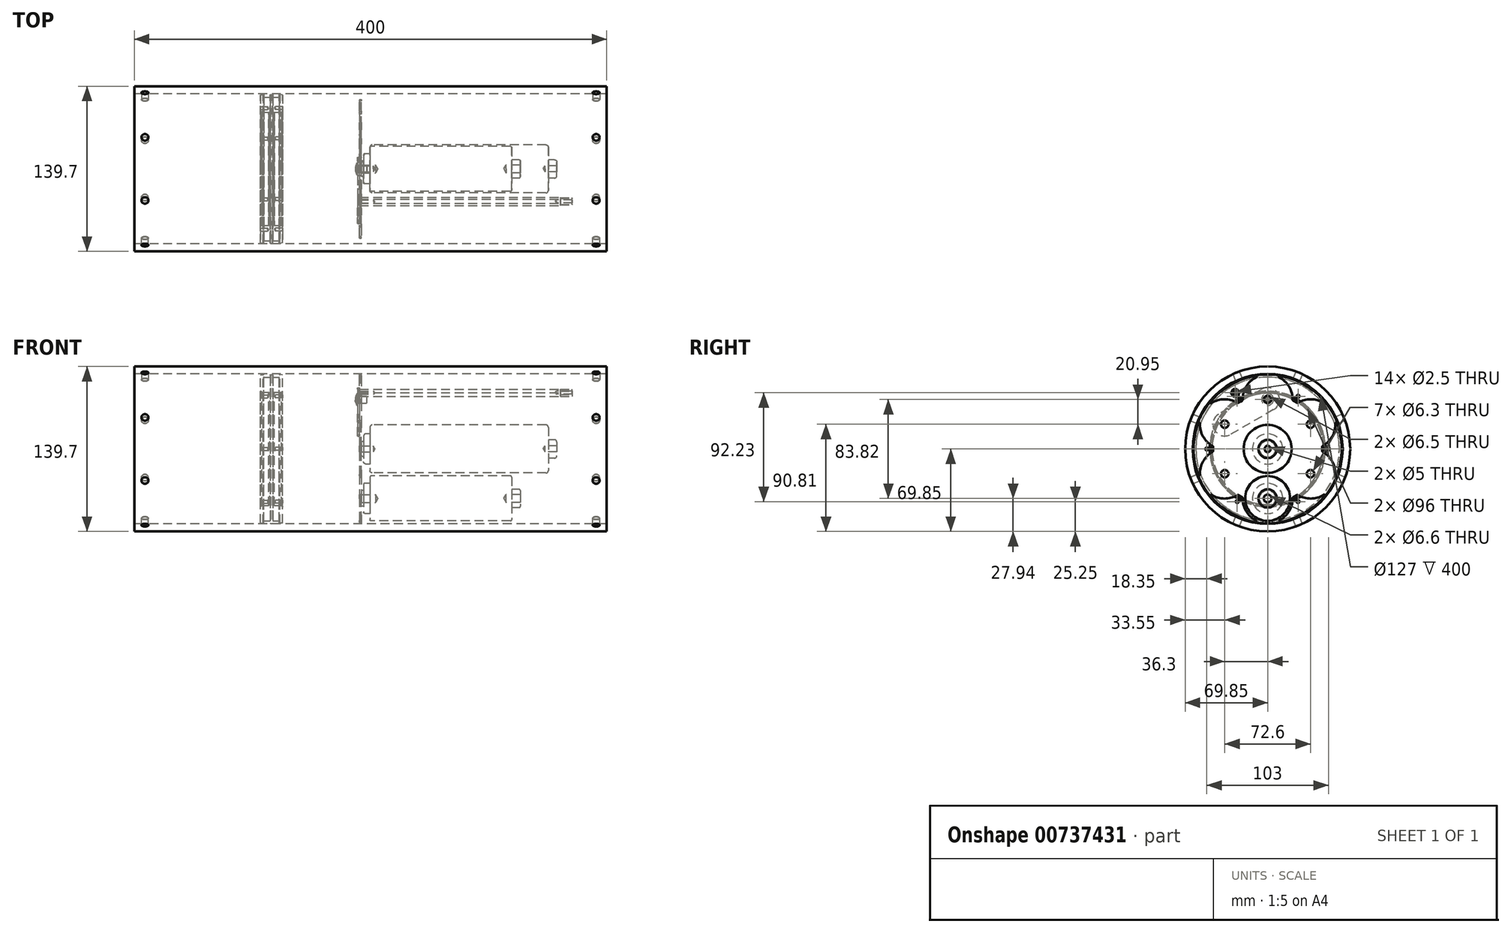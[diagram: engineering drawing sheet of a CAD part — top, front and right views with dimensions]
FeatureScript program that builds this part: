
annotation { "Feature Type Name" : "Feature", "Feature Type Description" : "" }
export const myFeature = defineFeature(function(context is Context, id is Id, definition is map)
    precondition{}
    {
        {
            var Q0;
            Q0=qCreatedBy(makeId("Front.planeOp"),FACE);
            var sketch = newSketch(context, id + "F0", { "sketchPlane" : qUnion([Q0])});
            skLineSegment(sketch, "E0", {"start": v(-82.75, 0) * mm, "end": v(82.75, 0) * mm});
            skLineSegment(sketch, "E1", {"start": v(-75.5, 20.32) * mm, "end": v(75.5, 20.32) * mm});
            skLineSegment(sketch, "E2", {"start": v(-82.75, 0) * mm, "end": v(-82.75, 6.75) * mm});
            skLineSegment(sketch, "E3", {"start": v(-82.75, 6.75) * mm, "end": v(-80.88, 6.75) * mm});
            skLineSegment(sketch, "E4", {"start": v(-80.88, 6.75) * mm, "end": v(-80.88, 12.8) * mm});
            skLineSegment(sketch, "E5", {"start": v(-80.88, 12.8) * mm, "end": v(-75.5, 12.8) * mm});
            skLineSegment(sketch, "E6", {"start": v(-75.5, 12.8) * mm, "end": v(-75.5, 20.32) * mm});
            skLineSegment(sketch, "E7", {"start": v(82.75, 0) * mm, "end": v(82.75, 7.75) * mm});
            skLineSegment(sketch, "E8", {"start": v(82.75, 7.75) * mm, "end": v(75.5, 7.75) * mm});
            skLineSegment(sketch, "E9", {"start": v(75.5, 7.75) * mm, "end": v(75.5, 20.32) * mm});
            skSolve(sketch);
        }
        {
            var Q0;
            Q0=makeQuery(id+"F0.imprint","IMPRINT",FACE,{"disambiguationData":[TD([[makeQuery(id+"F0.imprint","IMPRINT",EDGE,{"derivedFrom":sQuery(id+"F0.wireOp",EDGE,"E0")}),1.0]])]});
            var Q1;
            Q1=sQuery(id+"F0.wireOp",EDGE,"E0");
            revolve(context, id + "F1", {"entities" : qUnion([Q0]), "axis" : qUnion([Q1]), "revolveType" : RevolveType.FULL});
        }
        {
            var Q0;
            Q0=makeQuery(id+"F1.opRevolve","SWEPT_FACE",FACE,{"disambiguationData":[OSD([sQuery(id+"F0.wireOp",EDGE,"E1")])]});
            var Q1;
            Q1=makeQuery(id+"F1.opRevolve","SWEPT_EDGE",EDGE,{"disambiguationData":[OSD([sQuery(id+"F0.wireOp",EDGE,"E7"),sQuery(id+"F0.wireOp",EDGE,"E8")])]});
            var Q2;
            Q2=makeQuery(id+"F1.opRevolve","SWEPT_EDGE",EDGE,{"disambiguationData":[OSD([sQuery(id+"F0.wireOp",EDGE,"E4"),sQuery(id+"F0.wireOp",EDGE,"E5")])]});
            var Q3;
            Q3=makeQuery(id+"F1.opRevolve","SWEPT_EDGE",EDGE,{"disambiguationData":[OSD([sQuery(id+"F0.wireOp",EDGE,"E2"),sQuery(id+"F0.wireOp",EDGE,"E3")])]});
            fillet(context, id + "F2", {"entities" : qUnion([Q0, Q1, Q2, Q3]), "radius" : 2 * mm, "tangentPropagation" : true, "allowEdgeOverflow" : false});
        }
        {
            var Q0;
            Q0=makeQuery(id+"F1.opRevolve","SWEPT_FACE",FACE,{"disambiguationData":[OSD([sQuery(id+"F0.wireOp",EDGE,"E2")])]});
            var sketch = newSketch(context, id + "F3", { "sketchPlane" : qUnion([Q0])});
            skPoint(sketch, "E10", {"position": v(0, 0) * mm});
            skSolve(sketch);
        }
        {
            var Q0;
            Q0=makeQuery(id+"F1.opRevolve","SWEPT_FACE",FACE,{"disambiguationData":[OSD([sQuery(id+"F0.wireOp",EDGE,"E7")])]});
            var sketch = newSketch(context, id + "F4", { "sketchPlane" : qUnion([Q0])});
            skPoint(sketch, "E11", {"position": v(0, 0) * mm});
            skSolve(sketch);
        }
        {
            var Q0;
            Q0=sQuery(id+"F4.wireOp",VERTEX,"E11");
            var Q1;
            Q1=sQuery(id+"F3.wireOp",VERTEX,"E10");
            var Q2;
            Q2=makeQuery(id+"F1.opRevolve","SWEPT_BODY",BODY,{"disambiguationData":[OSD([sQuery(id+"F0.wireOp",EDGE,"E0"),sQuery(id+"F0.wireOp",EDGE,"E1"),sQuery(id+"F0.wireOp",EDGE,"E2"),sQuery(id+"F0.wireOp",EDGE,"E3"),sQuery(id+"F0.wireOp",EDGE,"E4"),sQuery(id+"F0.wireOp",EDGE,"E5"),sQuery(id+"F0.wireOp",EDGE,"E6"),sQuery(id+"F0.wireOp",EDGE,"E7"),sQuery(id+"F0.wireOp",EDGE,"E8"),sQuery(id+"F0.wireOp",EDGE,"E9")])]});
            hole(context, id + "F5", {"style" : HoleStyle.SIMPLE, "endStyle" : HoleEndStyle.BLIND, "standardTappedOrClearance" : lookupTablePath({ "standard" : "ISO", "engagement" : "75%", "pitch" : "1 mm", "size" : "M6", "type" : "Tapped" }), "standardBlindInLast" : lookupTablePath({ "standard" : "ISO", "engagement" : "75%", "pitch" : "1 mm", "size" : "M6", "type" : "Tapped" }), "holeDiameter" : 5 * mm, "holeDepth" : 10 * mm, "locations" : qUnion([Q0, Q1]), "scope" : qUnion([Q2]), "majorDiameter" : 6 * mm});
        }
        {
            var Q0;
            Q0=makeQuery(id+"F1.opRevolve","SWEPT_FACE",FACE,{"disambiguationData":[OSD([sQuery(id+"F0.wireOp",EDGE,"E2")])]});
            var sketch = newSketch(context, id + "F6", { "sketchPlane" : qUnion([Q0])});
            skCircle(sketch, "E12", {"center": v(0, 0) * mm, "radius": 63.5 * mm, "construction": true});
            skCircle(sketch, "E13.0", {"center": v(0, 0) * mm, "radius": 20.32 * mm, "construction": true});
            skLineSegment(sketch, "E14", {"start": v(0, 20.32) * mm, "end": v(0, 63.5) * mm, "construction": true});
            skCircle(sketch, "E15", {"center": v(0, 41.91) * mm, "radius": 20.32 * mm, "construction": true});
            skCircle(sketch, "E16", {"center": v(0, 41.91) * mm, "radius": 3.15 * mm});
            skCircle(sketch, "E17", {"center": v(0, 0) * mm, "radius": 3.15 * mm});
            skCircle(sketch, "E18", {"center": v(0, 0) * mm, "radius": 63 * mm});
            skCircle(sketch, "E19.1.0", {"center": v(-36.3, 20.96) * mm, "radius": 3.15 * mm});
            skCircle(sketch, "E19.2.0", {"center": v(-36.3, -20.96) * mm, "radius": 3.15 * mm});
            skCircle(sketch, "E19.3.0", {"center": v(0, -41.91) * mm, "radius": 3.15 * mm});
            skCircle(sketch, "E19.4.0", {"center": v(36.3, -20.96) * mm, "radius": 3.15 * mm});
            skCircle(sketch, "E19.5.0", {"center": v(36.3, 20.96) * mm, "radius": 3.15 * mm});
            skCircle(sketch, "E20", {"center": v(36.3, 20.96) * mm, "radius": 20.32 * mm, "construction": true});
            skCircle(sketch, "E21", {"center": v(0, 41.91) * mm, "radius": 10 * mm, "construction": true});
            skCircle(sketch, "E22", {"center": v(36.3, 20.96) * mm, "radius": 10 * mm, "construction": true});
            skLineSegment(sketch, "E23", {"start": v(-5, 33.25) * mm, "end": v(31.3, 12.3) * mm, "construction": true});
            skLineSegment(sketch, "E24", {"start": v(5, 50.57) * mm, "end": v(41.3, 29.62) * mm, "construction": true});
            skArc(sketch, "E25", {"start": v(0, 63) * mm, "mid": v(15.13, 56.6) * mm, "end": v(21.08, 41.29) * mm});
            skLineSegment(sketch, "E26", {"start": v(23.15, 40.1) * mm, "end": v(35.3, 61.15) * mm, "construction": true});
            skArc(sketch, "E27.MirrorCS", {"start": v(54.56, 31.5) * mm, "mid": v(41.45, 41.4) * mm, "end": v(25.22, 38.9) * mm});
            skLineSegment(sketch, "E28", {"start": v(21.08, 41.29) * mm, "end": v(25.22, 38.9) * mm});
            skLineSegment(sketch, "E29", {"start": v(9.66, 62.25) * mm, "end": v(9.43, 60.77) * mm});
            skCircle(sketch, "E30", {"center": v(0, -41.91) * mm, "radius": 19 * mm, "construction": true});
            skCircle(sketch, "E31", {"center": v(-36.3, -20.96) * mm, "radius": 19 * mm, "construction": true});
            skSolve(sketch);
        }
        {
            var Q0;
            Q0=qSketchRegion(id+"F6",true);
            extrude(context, id + "F7", {"entities" : qUnion([Q0]), "depth" : 1.6 * mm});
        }
        {
            var Q0;
            Q0=makeQuery(id+"F7.opExtrude","CAP_FACE",FACE,{"disambiguationData":[OSD([sQuery(id+"F6.wireOp",EDGE,"E16"),sQuery(id+"F6.wireOp",EDGE,"E17"),sQuery(id+"F6.wireOp",EDGE,"E18"),sQuery(id+"F6.wireOp",EDGE,"E19.1.0"),sQuery(id+"F6.wireOp",EDGE,"E19.2.0"),sQuery(id+"F6.wireOp",EDGE,"E19.3.0"),sQuery(id+"F6.wireOp",EDGE,"E19.4.0"),sQuery(id+"F6.wireOp",EDGE,"E19.5.0")])],"isStart":false});
            var sketch = newSketch(context, id + "F8", { "sketchPlane" : qUnion([Q0])});
            skArc(sketch, "E32.0", {"start": v(9.94, 60.51) * mm, "mid": v(18.13, 52.69) * mm, "end": v(21.09, 41.75) * mm});
            skArc(sketch, "E32.1", {"start": v(47.44, 38.86) * mm, "mid": v(36.57, 42.04) * mm, "end": v(25.62, 39.14) * mm});
            skArc(sketch, "E32.2", {"start": v(49.08, 39.5) * mm, "mid": v(31.5, 54.56) * mm, "end": v(9.66, 62.25) * mm});
            skLineSegment(sketch, "E32.3", {"start": v(9.66, 62.25) * mm, "end": v(9.52, 61.34) * mm});
            skLineSegment(sketch, "E32.4", {"start": v(21.49, 41.05) * mm, "end": v(24.81, 39.14) * mm});
            skLineSegment(sketch, "E32.5", {"start": v(23.15, 40.1) * mm, "end": v(35.3, 61.15) * mm, "construction": true});
            skLineSegment(sketch, "E33.MirrorCS", {"start": v(49.08, 39.5) * mm, "end": v(48.36, 38.92) * mm});
            skPoint(sketch, "E34.orphan", {"position": v(54.56, 31.5) * mm});
            skPoint(sketch, "E35.orphan", {"position": v(0, 63) * mm});
            skPoint(sketch, "E36.visualSharp", {"position": v(21.08, 41.29) * mm});
            skArc(sketch, "E36.filletArc", {"start": v(21.09, 41.75) * mm, "mid": v(21.2, 41.35) * mm, "end": v(21.49, 41.05) * mm});
            skPoint(sketch, "E37.visualSharp", {"position": v(25.22, 38.9) * mm});
            skArc(sketch, "E37.filletArc", {"start": v(24.81, 39.14) * mm, "mid": v(25.21, 39.03) * mm, "end": v(25.62, 39.14) * mm});
            skPoint(sketch, "E38.visualSharp", {"position": v(47.91, 38.56) * mm});
            skArc(sketch, "E38.filletArc", {"start": v(47.44, 38.86) * mm, "mid": v(47.9, 38.74) * mm, "end": v(48.36, 38.92) * mm});
            skPoint(sketch, "E39.visualSharp", {"position": v(9.43, 60.77) * mm});
            skArc(sketch, "E39.filletArc", {"start": v(9.52, 61.34) * mm, "mid": v(9.6, 60.86) * mm, "end": v(9.94, 60.51) * mm});
            skPoint(sketch, "E40.1.1", {"position": v(-54.56, 31.5) * mm});
            skArc(sketch, "E40.1.2", {"start": v(-47.44, 38.86) * mm, "mid": v(-36.57, 42.04) * mm, "end": v(-25.62, 39.14) * mm});
            skArc(sketch, "E40.1.3", {"start": v(-9.94, 60.51) * mm, "mid": v(-18.13, 52.69) * mm, "end": v(-21.09, 41.75) * mm});
            skArc(sketch, "E40.1.4", {"start": v(-9.66, 62.25) * mm, "mid": v(-31.5, 54.56) * mm, "end": v(-49.08, 39.5) * mm});
            skLineSegment(sketch, "E40.1.5", {"start": v(-23.15, 40.1) * mm, "end": v(-35.3, 61.15) * mm, "construction": true});
            skPoint(sketch, "E40.1.6", {"position": v(-25.22, 38.9) * mm});
            skPoint(sketch, "E40.1.7", {"position": v(-21.08, 41.29) * mm});
            skPoint(sketch, "E40.1.8", {"position": v(-9.43, 60.77) * mm});
            skPoint(sketch, "E40.1.9", {"position": v(-47.91, 38.56) * mm});
            skLineSegment(sketch, "E40.1.10", {"start": v(-24.81, 39.14) * mm, "end": v(-21.49, 41.05) * mm});
            skArc(sketch, "E40.1.11", {"start": v(-48.36, 38.92) * mm, "mid": v(-47.9, 38.74) * mm, "end": v(-47.44, 38.86) * mm});
            skLineSegment(sketch, "E40.1.12", {"start": v(-49.08, 39.5) * mm, "end": v(-48.36, 38.92) * mm});
            skArc(sketch, "E40.1.13", {"start": v(-25.62, 39.14) * mm, "mid": v(-25.21, 39.03) * mm, "end": v(-24.81, 39.14) * mm});
            skArc(sketch, "E40.1.14", {"start": v(-21.49, 41.05) * mm, "mid": v(-21.2, 41.35) * mm, "end": v(-21.09, 41.75) * mm});
            skLineSegment(sketch, "E40.1.15", {"start": v(-9.66, 62.25) * mm, "end": v(-9.52, 61.34) * mm});
            skArc(sketch, "E40.1.16", {"start": v(-9.94, 60.51) * mm, "mid": v(-9.6, 60.86) * mm, "end": v(-9.52, 61.34) * mm});
            skPoint(sketch, "E40.2.0", {"position": v(-54.56, 31.5) * mm});
            skPoint(sketch, "E40.2.1", {"position": v(-54.56, -31.5) * mm});
            skArc(sketch, "E40.2.2", {"start": v(-57.37, -21.65) * mm, "mid": v(-54.7, -10.65) * mm, "end": v(-46.7, -2.61) * mm});
            skArc(sketch, "E40.2.3", {"start": v(-57.37, 21.65) * mm, "mid": v(-54.7, 10.65) * mm, "end": v(-46.7, 2.61) * mm});
            skArc(sketch, "E40.2.4", {"start": v(-58.75, 22.76) * mm, "mid": v(-63, 0) * mm, "end": v(-58.75, -22.76) * mm});
            skLineSegment(sketch, "E40.2.5", {"start": v(-46.3, 0) * mm, "end": v(-70.6, 0) * mm, "construction": true});
            skPoint(sketch, "E40.2.6", {"position": v(-46.3, -2.4) * mm});
            skPoint(sketch, "E40.2.7", {"position": v(-46.3, 2.4) * mm});
            skPoint(sketch, "E40.2.8", {"position": v(-57.35, 22.22) * mm});
            skPoint(sketch, "E40.2.9", {"position": v(-57.35, -22.22) * mm});
            skLineSegment(sketch, "E40.2.10", {"start": v(-46.3, -1.92) * mm, "end": v(-46.3, 1.92) * mm});
            skArc(sketch, "E40.2.11", {"start": v(-57.88, -22.42) * mm, "mid": v(-57.5, -22.12) * mm, "end": v(-57.37, -21.65) * mm});
            skLineSegment(sketch, "E40.2.12", {"start": v(-58.75, -22.76) * mm, "end": v(-57.88, -22.42) * mm});
            skArc(sketch, "E40.2.13", {"start": v(-46.7, -2.61) * mm, "mid": v(-46.4, -2.32) * mm, "end": v(-46.3, -1.92) * mm});
            skArc(sketch, "E40.2.14", {"start": v(-46.3, 1.92) * mm, "mid": v(-46.4, 2.32) * mm, "end": v(-46.7, 2.61) * mm});
            skLineSegment(sketch, "E40.2.15", {"start": v(-58.75, 22.76) * mm, "end": v(-57.88, 22.42) * mm});
            skArc(sketch, "E40.2.16", {"start": v(-57.37, 21.65) * mm, "mid": v(-57.5, 22.12) * mm, "end": v(-57.88, 22.42) * mm});
            skPoint(sketch, "E40.3.0", {"position": v(-54.56, -31.5) * mm});
            skPoint(sketch, "E40.3.1", {"position": v(0, -63) * mm});
            skArc(sketch, "E40.3.2", {"start": v(-9.94, -60.51) * mm, "mid": v(-18.13, -52.69) * mm, "end": v(-21.09, -41.75) * mm});
            skArc(sketch, "E40.3.3", {"start": v(-47.44, -38.86) * mm, "mid": v(-36.57, -42.04) * mm, "end": v(-25.62, -39.14) * mm});
            skArc(sketch, "E40.3.4", {"start": v(-49.08, -39.5) * mm, "mid": v(-31.5, -54.56) * mm, "end": v(-9.66, -62.25) * mm});
            skLineSegment(sketch, "E40.3.5", {"start": v(-23.15, -40.1) * mm, "end": v(-35.3, -61.15) * mm, "construction": true});
            skPoint(sketch, "E40.3.6", {"position": v(-21.08, -41.29) * mm});
            skPoint(sketch, "E40.3.7", {"position": v(-25.22, -38.9) * mm});
            skPoint(sketch, "E40.3.8", {"position": v(-47.91, -38.56) * mm});
            skPoint(sketch, "E40.3.9", {"position": v(-9.43, -60.77) * mm});
            skLineSegment(sketch, "E40.3.10", {"start": v(-21.49, -41.05) * mm, "end": v(-24.81, -39.14) * mm});
            skArc(sketch, "E40.3.11", {"start": v(-9.52, -61.34) * mm, "mid": v(-9.6, -60.86) * mm, "end": v(-9.94, -60.51) * mm});
            skLineSegment(sketch, "E40.3.12", {"start": v(-9.66, -62.25) * mm, "end": v(-9.52, -61.34) * mm});
            skArc(sketch, "E40.3.13", {"start": v(-21.09, -41.75) * mm, "mid": v(-21.2, -41.35) * mm, "end": v(-21.49, -41.05) * mm});
            skArc(sketch, "E40.3.14", {"start": v(-24.81, -39.14) * mm, "mid": v(-25.21, -39.03) * mm, "end": v(-25.62, -39.14) * mm});
            skLineSegment(sketch, "E40.3.15", {"start": v(-49.08, -39.5) * mm, "end": v(-48.36, -38.92) * mm});
            skArc(sketch, "E40.3.16", {"start": v(-47.44, -38.86) * mm, "mid": v(-47.9, -38.74) * mm, "end": v(-48.36, -38.92) * mm});
            skPoint(sketch, "E40.4.0", {"position": v(0, -63) * mm});
            skPoint(sketch, "E40.4.1", {"position": v(54.56, -31.5) * mm});
            skArc(sketch, "E40.4.2", {"start": v(47.44, -38.86) * mm, "mid": v(36.57, -42.04) * mm, "end": v(25.62, -39.14) * mm});
            skArc(sketch, "E40.4.3", {"start": v(9.94, -60.51) * mm, "mid": v(18.13, -52.69) * mm, "end": v(21.09, -41.75) * mm});
            skArc(sketch, "E40.4.4", {"start": v(9.66, -62.25) * mm, "mid": v(31.5, -54.56) * mm, "end": v(49.08, -39.5) * mm});
            skLineSegment(sketch, "E40.4.5", {"start": v(23.15, -40.1) * mm, "end": v(35.3, -61.15) * mm, "construction": true});
            skPoint(sketch, "E40.4.6", {"position": v(25.22, -38.9) * mm});
            skPoint(sketch, "E40.4.7", {"position": v(21.08, -41.29) * mm});
            skPoint(sketch, "E40.4.8", {"position": v(9.43, -60.77) * mm});
            skPoint(sketch, "E40.4.9", {"position": v(47.91, -38.56) * mm});
            skLineSegment(sketch, "E40.4.10", {"start": v(24.81, -39.14) * mm, "end": v(21.49, -41.05) * mm});
            skArc(sketch, "E40.4.11", {"start": v(48.36, -38.92) * mm, "mid": v(47.9, -38.74) * mm, "end": v(47.44, -38.86) * mm});
            skLineSegment(sketch, "E40.4.12", {"start": v(49.08, -39.5) * mm, "end": v(48.36, -38.92) * mm});
            skArc(sketch, "E40.4.13", {"start": v(25.62, -39.14) * mm, "mid": v(25.21, -39.03) * mm, "end": v(24.81, -39.14) * mm});
            skArc(sketch, "E40.4.14", {"start": v(21.49, -41.05) * mm, "mid": v(21.2, -41.35) * mm, "end": v(21.09, -41.75) * mm});
            skLineSegment(sketch, "E40.4.15", {"start": v(9.66, -62.25) * mm, "end": v(9.52, -61.34) * mm});
            skArc(sketch, "E40.4.16", {"start": v(9.94, -60.51) * mm, "mid": v(9.6, -60.86) * mm, "end": v(9.52, -61.34) * mm});
            skPoint(sketch, "E40.5.0", {"position": v(54.56, -31.5) * mm});
            skArc(sketch, "E40.5.2", {"start": v(57.37, 21.65) * mm, "mid": v(54.7, 10.65) * mm, "end": v(46.7, 2.61) * mm});
            skArc(sketch, "E40.5.3", {"start": v(57.37, -21.65) * mm, "mid": v(54.7, -10.65) * mm, "end": v(46.7, -2.61) * mm});
            skArc(sketch, "E40.5.4", {"start": v(58.75, -22.76) * mm, "mid": v(63, 0) * mm, "end": v(58.75, 22.76) * mm});
            skLineSegment(sketch, "E40.5.5", {"start": v(46.3, 0) * mm, "end": v(70.6, 0) * mm, "construction": true});
            skPoint(sketch, "E40.5.6", {"position": v(46.3, 2.4) * mm});
            skPoint(sketch, "E40.5.7", {"position": v(46.3, -2.4) * mm});
            skPoint(sketch, "E40.5.8", {"position": v(57.35, -22.22) * mm});
            skPoint(sketch, "E40.5.9", {"position": v(57.35, 22.22) * mm});
            skLineSegment(sketch, "E40.5.10", {"start": v(46.3, 1.92) * mm, "end": v(46.3, -1.92) * mm});
            skArc(sketch, "E40.5.11", {"start": v(57.88, 22.42) * mm, "mid": v(57.5, 22.12) * mm, "end": v(57.37, 21.65) * mm});
            skLineSegment(sketch, "E40.5.12", {"start": v(58.75, 22.76) * mm, "end": v(57.88, 22.42) * mm});
            skArc(sketch, "E40.5.13", {"start": v(46.7, 2.61) * mm, "mid": v(46.4, 2.32) * mm, "end": v(46.3, 1.92) * mm});
            skArc(sketch, "E40.5.14", {"start": v(46.3, -1.92) * mm, "mid": v(46.4, -2.32) * mm, "end": v(46.7, -2.61) * mm});
            skLineSegment(sketch, "E40.5.15", {"start": v(58.75, -22.76) * mm, "end": v(57.88, -22.42) * mm});
            skArc(sketch, "E40.5.16", {"start": v(57.37, -21.65) * mm, "mid": v(57.5, -22.12) * mm, "end": v(57.88, -22.42) * mm});
            skSolve(sketch);
        }
        {
            var Q0;
            Q0=qSketchRegion(id+"F8",true);
            extrude(context, id + "F9", {"entities" : qUnion([Q0]), "operationType" : NewBodyOperationType.REMOVE, "oppositeDirection" : true, "depth" : 25 * mm});
        }
        {
            var Q0;
            Q0=makeQuery(id+"F9.boolean.opBoolean","COPY",EDGE,{"derivedFrom":makeQuery(id+"F9.opExtrude","SWEPT_EDGE",EDGE,{"disambiguationData":[OSD([sQuery(id+"F6.wireOp",EDGE,"E18"),sQuery(id+"F8.wireOp",EDGE,"E32.2"),sQuery(id+"F8.wireOp",EDGE,"E32.3")])]})});
            var Q1;
            Q1=makeQuery(id+"F9.boolean.opBoolean","COPY",EDGE,{"derivedFrom":makeQuery(id+"F9.opExtrude","SWEPT_EDGE",EDGE,{"disambiguationData":[OSD([sQuery(id+"F6.wireOp",EDGE,"E18"),sQuery(id+"F8.wireOp",EDGE,"E32.2"),sQuery(id+"F8.wireOp",EDGE,"E33.MirrorCS")])]})});
            var Q2;
            Q2=makeQuery(id+"FGbRxVnL68Y7Bjd_2.1.F9.boolean.opBoolean","COPY",EDGE,{"derivedFrom":makeQuery(id+"FGbRxVnL68Y7Bjd_2.1.F9.opExtrude","SWEPT_EDGE",EDGE,{"disambiguationData":[OSD([sQuery(id+"F6.wireOp",EDGE,"E18"),sQuery(id+"F8.wireOp",EDGE,"E32.2"),sQuery(id+"F8.wireOp",EDGE,"E32.3")])]})});
            var Q3;
            Q3=makeQuery(id+"FGbRxVnL68Y7Bjd_2.1.F9.boolean.opBoolean","COPY",EDGE,{"derivedFrom":makeQuery(id+"FGbRxVnL68Y7Bjd_2.1.F9.opExtrude","SWEPT_EDGE",EDGE,{"disambiguationData":[OSD([sQuery(id+"F6.wireOp",EDGE,"E18"),sQuery(id+"F8.wireOp",EDGE,"E32.2"),sQuery(id+"F8.wireOp",EDGE,"E33.MirrorCS")])]})});
            var Q4;
            Q4=makeQuery(id+"FGbRxVnL68Y7Bjd_2.2.F9.boolean.opBoolean","COPY",EDGE,{"derivedFrom":makeQuery(id+"FGbRxVnL68Y7Bjd_2.2.F9.opExtrude","SWEPT_EDGE",EDGE,{"disambiguationData":[OSD([sQuery(id+"F6.wireOp",EDGE,"E18"),sQuery(id+"F8.wireOp",EDGE,"E32.2"),sQuery(id+"F8.wireOp",EDGE,"E32.3")])]})});
            var Q5;
            Q5=makeQuery(id+"FGbRxVnL68Y7Bjd_2.2.F9.boolean.opBoolean","COPY",EDGE,{"derivedFrom":makeQuery(id+"FGbRxVnL68Y7Bjd_2.2.F9.opExtrude","SWEPT_EDGE",EDGE,{"disambiguationData":[OSD([sQuery(id+"F6.wireOp",EDGE,"E18"),sQuery(id+"F8.wireOp",EDGE,"E32.2"),sQuery(id+"F8.wireOp",EDGE,"E33.MirrorCS")])]})});
            var Q6;
            Q6=makeQuery(id+"FGbRxVnL68Y7Bjd_2.3.F9.boolean.opBoolean","COPY",EDGE,{"derivedFrom":makeQuery(id+"FGbRxVnL68Y7Bjd_2.3.F9.opExtrude","SWEPT_EDGE",EDGE,{"disambiguationData":[OSD([sQuery(id+"F6.wireOp",EDGE,"E18"),sQuery(id+"F8.wireOp",EDGE,"E32.2"),sQuery(id+"F8.wireOp",EDGE,"E32.3")])]})});
            var Q7;
            Q7=makeQuery(id+"FGbRxVnL68Y7Bjd_2.4.F9.boolean.opBoolean","COPY",EDGE,{"derivedFrom":makeQuery(id+"FGbRxVnL68Y7Bjd_2.4.F9.opExtrude","SWEPT_EDGE",EDGE,{"disambiguationData":[OSD([sQuery(id+"F6.wireOp",EDGE,"E18"),sQuery(id+"F8.wireOp",EDGE,"E32.2"),sQuery(id+"F8.wireOp",EDGE,"E32.3")])]})});
            var Q8;
            Q8=makeQuery(id+"FGbRxVnL68Y7Bjd_2.3.F9.boolean.opBoolean","COPY",EDGE,{"derivedFrom":makeQuery(id+"FGbRxVnL68Y7Bjd_2.3.F9.opExtrude","SWEPT_EDGE",EDGE,{"disambiguationData":[OSD([sQuery(id+"F6.wireOp",EDGE,"E18"),sQuery(id+"F8.wireOp",EDGE,"E32.2"),sQuery(id+"F8.wireOp",EDGE,"E33.MirrorCS")])]})});
            var Q9;
            Q9=makeQuery(id+"FGbRxVnL68Y7Bjd_2.4.F9.boolean.opBoolean","COPY",EDGE,{"derivedFrom":makeQuery(id+"FGbRxVnL68Y7Bjd_2.4.F9.opExtrude","SWEPT_EDGE",EDGE,{"disambiguationData":[OSD([sQuery(id+"F6.wireOp",EDGE,"E18"),sQuery(id+"F8.wireOp",EDGE,"E32.2"),sQuery(id+"F8.wireOp",EDGE,"E33.MirrorCS")])]})});
            var Q10;
            Q10=makeQuery(id+"FGbRxVnL68Y7Bjd_2.5.F9.boolean.opBoolean","COPY",EDGE,{"derivedFrom":makeQuery(id+"FGbRxVnL68Y7Bjd_2.5.F9.opExtrude","SWEPT_EDGE",EDGE,{"disambiguationData":[OSD([sQuery(id+"F6.wireOp",EDGE,"E18"),sQuery(id+"F8.wireOp",EDGE,"E32.2"),sQuery(id+"F8.wireOp",EDGE,"E32.3")])]})});
            var Q11;
            Q11=makeQuery(id+"FGbRxVnL68Y7Bjd_2.5.F9.boolean.opBoolean","COPY",EDGE,{"derivedFrom":makeQuery(id+"FGbRxVnL68Y7Bjd_2.5.F9.opExtrude","SWEPT_EDGE",EDGE,{"disambiguationData":[OSD([sQuery(id+"F6.wireOp",EDGE,"E18"),sQuery(id+"F8.wireOp",EDGE,"E32.2"),sQuery(id+"F8.wireOp",EDGE,"E33.MirrorCS")])]})});
            fillet(context, id + "F10", {"entities" : qUnion([Q0, Q1, Q2, Q3, Q4, Q5, Q6, Q7, Q8, Q9, Q10, Q11]), "radius" : .8 * mm, "tangentPropagation" : true, "allowEdgeOverflow" : false});
        }
        {
            var Q0;
            Q0=makeQuery(id+"F7.opExtrude","CAP_FACE",FACE,{"disambiguationData":[OSD([sQuery(id+"F6.wireOp",EDGE,"E16"),sQuery(id+"F6.wireOp",EDGE,"E17"),sQuery(id+"F6.wireOp",EDGE,"E18"),sQuery(id+"F6.wireOp",EDGE,"E19.1.0"),sQuery(id+"F6.wireOp",EDGE,"E19.2.0"),sQuery(id+"F6.wireOp",EDGE,"E19.3.0"),sQuery(id+"F6.wireOp",EDGE,"E19.4.0"),sQuery(id+"F6.wireOp",EDGE,"E19.5.0")])],"isStart":false});
            var sketch = newSketch(context, id + "F11", { "sketchPlane" : qUnion([Q0])});
            skLineSegment(sketch, "E41.0", {"start": v(-5, 33.25) * mm, "end": v(31.3, 12.3) * mm});
            skLineSegment(sketch, "E41.1", {"start": v(5, 50.57) * mm, "end": v(41.3, 29.62) * mm});
            skArc(sketch, "E41.2", {"start": v(5, 50.57) * mm, "mid": v(-8.66, 46.91) * mm, "end": v(-5, 33.25) * mm});
            skArc(sketch, "E41.3", {"start": v(31.3, 12.3) * mm, "mid": v(44.96, 15.96) * mm, "end": v(41.3, 29.62) * mm});
            skPoint(sketch, "E41.4", {"position": v(0, 41.91) * mm});
            skPoint(sketch, "E41.5", {"position": v(36.3, 20.96) * mm});
            skCircle(sketch, "E42", {"center": v(0, 41.91) * mm, "radius": 3.25 * mm});
            skCircle(sketch, "E43", {"center": v(36.3, 20.96) * mm, "radius": 3.25 * mm});
            skSolve(sketch);
        }
        {
            var Q0;
            Q0=makeQuery(id+"F11.imprint","IMPRINT",FACE,{"disambiguationData":[TD([[makeQuery(id+"F11.imprint","IMPRINT",EDGE,{"derivedFrom":sQuery(id+"F11.wireOp",EDGE,"E41.0")}),1.0]])]});
            extrude(context, id + "F12", {"entities" : qUnion([Q0]), "depth" : 1.6 * mm});
        }
        {
            var Q0;
            Q0=qCreatedBy(makeId("Front.planeOp"),FACE);
            var sketch = newSketch(context, id + "F13", { "sketchPlane" : qUnion([Q0])});
            skPoint(sketch, "E44.0", {"position": v(-82.75, 41.91) * mm});
            skLineSegment(sketch, "E45", {"start": v(-82.75, 41.91) * mm, "end": v(-64.6, 41.91) * mm});
            skLineSegment(sketch, "E46", {"start": v(-64.6, 41.91) * mm, "end": v(-82.75, 41.91) * mm});
            skLineSegment(sketch, "E47", {"start": v(-82.75, 41.91) * mm, "end": v(-93.65, 41.91) * mm});
            skLineSegment(sketch, "E48.0", {"start": v(-85.95, 50.57) * mm, "end": v(-85.95, 29.62) * mm, "construction": true});
            skLineSegment(sketch, "E49", {"start": v(-85.95, 46.91) * mm, "end": v(-86.45, 46.91) * mm});
            skLineSegment(sketch, "E50", {"start": v(-77.95, 41.91) * mm, "end": v(-77.95, 44.91) * mm});
            skLineSegment(sketch, "E51", {"start": v(-77.95, 44.91) * mm, "end": v(-85.95, 44.91) * mm});
            skLineSegment(sketch, "E52", {"start": v(-85.95, 44.91) * mm, "end": v(-85.95, 46.91) * mm});
            skArc(sketch, "E53", {"start": v(-86.45, 46.91) * mm, "mid": v(-87.57, 44.52) * mm, "end": v(-87.95, 41.91) * mm});
            skSolve(sketch);
        }
        {
            var Q0;
            Q0=makeQuery(id+"F13.imprint","IMPRINT",FACE,{"disambiguationData":[TD([[makeQuery(id+"F13.imprint","IMPRINT",EDGE,{"derivedFrom":sQuery(id+"F13.wireOp",EDGE,"E49")}),1.0]])]});
            var Q1;
            Q1=sQuery(id+"F13.wireOp",EDGE,"E46");
            revolve(context, id + "F14", {"entities" : qUnion([Q0]), "axis" : qUnion([Q1]), "revolveType" : RevolveType.FULL});
        }
        {
            var Q0;
            Q0=makeQuery(id+"F12.opExtrude","CAP_FACE",FACE,{"disambiguationData":[OSD([sQuery(id+"F11.wireOp",EDGE,"E41.0"),sQuery(id+"F11.wireOp",EDGE,"E41.1"),sQuery(id+"F11.wireOp",EDGE,"E41.2"),sQuery(id+"F11.wireOp",EDGE,"E41.3"),sQuery(id+"F11.wireOp",EDGE,"E42"),sQuery(id+"F11.wireOp",EDGE,"E43")])],"isStart":false});
            var sketch = newSketch(context, id + "F15", { "sketchPlane" : qUnion([Q0])});
            skLineSegment(sketch, "E54", {"start": v(0, 44.41) * mm, "end": v(0.5, 44.41) * mm});
            skLineSegment(sketch, "E55", {"start": v(0.5, 44.41) * mm, "end": v(0.5, 42.41) * mm});
            skLineSegment(sketch, "E56", {"start": v(0.5, 42.41) * mm, "end": v(2.5, 42.41) * mm});
            skLineSegment(sketch, "E57", {"start": v(2.5, 42.41) * mm, "end": v(2.5, 41.91) * mm});
            skLineSegment(sketch, "E58", {"start": v(2.5, 41.91) * mm, "end": v(0, 41.91) * mm});
            skLineSegment(sketch, "E59", {"start": v(0, 41.91) * mm, "end": v(0, 44.41) * mm, "construction": true});
            skLineSegment(sketch, "E60.1.0", {"start": v(-2.5, 41.91) * mm, "end": v(-2.5, 42.41) * mm});
            skLineSegment(sketch, "E60.1.1", {"start": v(-2.5, 42.41) * mm, "end": v(-0.5, 42.41) * mm});
            skLineSegment(sketch, "E60.1.2", {"start": v(-0.5, 42.41) * mm, "end": v(-0.5, 44.41) * mm});
            skLineSegment(sketch, "E60.1.3", {"start": v(-0.5, 44.41) * mm, "end": v(0, 44.41) * mm});
            skLineSegment(sketch, "E60.2.0", {"start": v(0, 39.41) * mm, "end": v(-0.5, 39.41) * mm});
            skLineSegment(sketch, "E60.2.1", {"start": v(-0.5, 39.41) * mm, "end": v(-0.5, 41.41) * mm});
            skLineSegment(sketch, "E60.2.2", {"start": v(-0.5, 41.41) * mm, "end": v(-2.5, 41.41) * mm});
            skLineSegment(sketch, "E60.2.3", {"start": v(-2.5, 41.41) * mm, "end": v(-2.5, 41.91) * mm});
            skLineSegment(sketch, "E60.3.0", {"start": v(2.5, 41.91) * mm, "end": v(2.5, 41.41) * mm});
            skLineSegment(sketch, "E60.3.1", {"start": v(2.5, 41.41) * mm, "end": v(0.5, 41.41) * mm});
            skLineSegment(sketch, "E60.3.2", {"start": v(0.5, 41.41) * mm, "end": v(0.5, 39.41) * mm});
            skLineSegment(sketch, "E60.3.3", {"start": v(0.5, 39.41) * mm, "end": v(0, 39.41) * mm});
            skPoint(sketch, "E60.center", {"position": v(0, 41.91) * mm});
            skSolve(sketch);
        }
        {
            var Q0;
            Q0=qSketchRegion(id+"F15",true);
            extrude(context, id + "F16", {"entities" : qUnion([Q0]), "operationType" : NewBodyOperationType.REMOVE, "depth" : 25 * mm});
        }
        {
            var Q0;
            Q0=qCreatedBy(makeId("Right.planeOp"),FACE);
            var sketch = newSketch(context, id + "F17", { "sketchPlane" : qUnion([Q0])});
            skCircle(sketch, "E61", {"center": v(0, 0) * mm, "radius": 69.85 * mm});
            skCircle(sketch, "E62", {"center": v(0, 0) * mm, "radius": 63.5 * mm});
            skSolve(sketch);
        }
        {
            var Q0;
            Q0=makeQuery(id+"F17.imprint","IMPRINT",FACE,{"disambiguationData":[TD([[makeQuery(id+"F17.imprint","IMPRINT",EDGE,{"derivedFrom":sQuery(id+"F17.wireOp",EDGE,"E61")}),1.0]])]});
            var Q1;
            Q1=qSketchRegion(id+"F20",true);
            extrude(context, id + "F18", {"entities" : qUnion([Q0, Q1]), "depth" : 125 * mm, "hasSecondDirection" : true, "secondDirectionOppositeDirection" : true, "secondDirectionDepth" : (400 - 125) * mm});
        }
        {
            var Q0;
            Q0=makeQuery(id+"F18.opExtrude","CAP_FACE",FACE,{"disambiguationData":[OSD([sQuery(id+"F17.wireOp",EDGE,"E61"),sQuery(id+"F17.wireOp",EDGE,"E62")])],"isStart":false});
            cPlane(context, id + "F19", {"entities" : qUnion([Q0]), "cplaneType" : CPlaneType.OFFSET, "offset" : 29.25 * mm + 3 / 406.4 * mm, "oppositeDirection" : true, "width" : 150 * mm, "height" : 150 * mm});
        }
        {
            var Q0;
            Q0=qCreatedBy(id+"F19.planeOp",FACE);
            var sketch = newSketch(context, id + "F20", { "sketchPlane" : qUnion([Q0])});
            skCircle(sketch, "E63", {"center": v(0, 0) * mm, "radius": 55 * mm, "construction": true});
            skCircle(sketch, "E64.cCircle", {"center": v(-27.5, 47.63) * mm, "radius": 3 * mm, "construction": true});
            skLineSegment(sketch, "E64.0", {"start": v(-29.23, 50.63) * mm, "end": v(-25.77, 50.63) * mm});
            skLineSegment(sketch, "E64.1", {"start": v(-25.77, 50.63) * mm, "end": v(-24.04, 47.63) * mm});
            skLineSegment(sketch, "E64.2", {"start": v(-24.04, 47.63) * mm, "end": v(-25.77, 44.63) * mm});
            skLineSegment(sketch, "E64.3", {"start": v(-25.77, 44.63) * mm, "end": v(-29.23, 44.63) * mm});
            skLineSegment(sketch, "E64.4", {"start": v(-29.23, 44.63) * mm, "end": v(-30.96, 47.63) * mm});
            skLineSegment(sketch, "E64.5", {"start": v(-30.96, 47.63) * mm, "end": v(-29.23, 50.63) * mm});
            skPoint(sketch, "E64.0.midPoint", {"position": v(-27.5, 50.63) * mm});
            skLineSegment(sketch, "E65", {"start": v(0, 0) * mm, "end": v(-27.5, 47.63) * mm, "construction": true});
            skLineSegment(sketch, "E66", {"start": v(0, 0) * mm, "end": v(0, 55) * mm, "construction": true});
            skSolve(sketch);
        }
        {
            var Q0;
            Q0=qSketchRegion(id+"F20",true);
            extrude(context, id + "F21", {"entities" : qUnion([Q0]), "oppositeDirection" : true, "depth" : 180 * mm});
        }
        {
            var Q0;
            Q0=qCreatedBy(makeId("Front.planeOp"),FACE);
            var sketch = newSketch(context, id + "F22", { "sketchPlane" : qUnion([Q0])});
            skLineSegment(sketch, "E67", {"start": v(-82.75, -41.91) * mm, "end": v(51.75, -41.91) * mm});
            skLineSegment(sketch, "E68", {"start": v(-75.5, -22.91) * mm, "end": v(44.5, -22.91) * mm});
            skLineSegment(sketch, "E69", {"start": v(-82.75, -41.91) * mm, "end": v(-82.75, -35.16) * mm});
            skLineSegment(sketch, "E70", {"start": v(-82.75, -35.16) * mm, "end": v(-80.88, -35.16) * mm});
            skLineSegment(sketch, "E71", {"start": v(-80.88, -35.16) * mm, "end": v(-80.88, -29.11) * mm});
            skLineSegment(sketch, "E72", {"start": v(-80.88, -29.11) * mm, "end": v(-75.5, -29.11) * mm});
            skLineSegment(sketch, "E73", {"start": v(-75.5, -29.11) * mm, "end": v(-75.5, -22.91) * mm});
            skLineSegment(sketch, "E74", {"start": v(51.75, -41.91) * mm, "end": v(51.75, -34.16) * mm});
            skLineSegment(sketch, "E75", {"start": v(51.75, -34.16) * mm, "end": v(44.5, -34.16) * mm});
            skLineSegment(sketch, "E76", {"start": v(44.5, -34.16) * mm, "end": v(44.5, -22.91) * mm});
            skLineSegment(sketch, "E77.0", {"start": v(-82.75, -45.06) * mm, "end": v(-82.75, -38.76) * mm, "construction": true});
            skSolve(sketch);
        }
        {
            var Q0;
            Q0=qSketchRegion(id+"F22",true);
            var Q1;
            Q1=sQuery(id+"F22.wireOp",EDGE,"E67");
            revolve(context, id + "F23", {"entities" : qUnion([Q0]), "axis" : qUnion([Q1]), "revolveType" : RevolveType.FULL});
        }
        {
            var Q0;
            Q0=makeQuery(id+"F23.opRevolve","SWEPT_EDGE",EDGE,{"disambiguationData":[OSD([sQuery(id+"F22.wireOp",EDGE,"E68"),sQuery(id+"F22.wireOp",EDGE,"E76")])]});
            var Q1;
            Q1=makeQuery(id+"F23.opRevolve","SWEPT_EDGE",EDGE,{"disambiguationData":[OSD([sQuery(id+"F22.wireOp",EDGE,"E74"),sQuery(id+"F22.wireOp",EDGE,"E75")])]});
            var Q2;
            Q2=makeQuery(id+"F23.opRevolve","SWEPT_EDGE",EDGE,{"disambiguationData":[OSD([sQuery(id+"F22.wireOp",EDGE,"E68"),sQuery(id+"F22.wireOp",EDGE,"E73")])]});
            var Q3;
            Q3=makeQuery(id+"F23.opRevolve","SWEPT_EDGE",EDGE,{"disambiguationData":[OSD([sQuery(id+"F22.wireOp",EDGE,"E71"),sQuery(id+"F22.wireOp",EDGE,"E72")])]});
            var Q4;
            Q4=makeQuery(id+"F23.opRevolve","SWEPT_EDGE",EDGE,{"disambiguationData":[OSD([sQuery(id+"F22.wireOp",EDGE,"E69"),sQuery(id+"F22.wireOp",EDGE,"E70")])]});
            fillet(context, id + "F24", {"entities" : qUnion([Q0, Q1, Q2, Q3, Q4]), "radius" : 1 * mm, "tangentPropagation" : true, "allowEdgeOverflow" : false});
        }
        {
            var Q0;
            Q0=makeQuery(id+"F23.opRevolve","SWEPT_FACE",FACE,{"disambiguationData":[OSD([sQuery(id+"F22.wireOp",EDGE,"E74")])]});
            var sketch = newSketch(context, id + "F25", { "sketchPlane" : qUnion([Q0])});
            skPoint(sketch, "E78", {"position": v(0, -41.91) * mm});
            skSolve(sketch);
        }
        {
            var Q0;
            Q0=makeQuery(id+"F23.opRevolve","SWEPT_FACE",FACE,{"disambiguationData":[OSD([sQuery(id+"F22.wireOp",EDGE,"E69")])]});
            var sketch = newSketch(context, id + "F26", { "sketchPlane" : qUnion([Q0])});
            skPoint(sketch, "E79", {"position": v(0, -41.91) * mm});
            skSolve(sketch);
        }
        {
            var Q0;
            Q0=sQuery(id+"F26.wireOp",VERTEX,"E79");
            var Q1;
            Q1=sQuery(id+"F25.wireOp",VERTEX,"E78");
            var Q2;
            Q2=makeQuery(id+"F23.opRevolve","SWEPT_BODY",BODY,{"disambiguationData":[OSD([sQuery(id+"F22.wireOp",EDGE,"E67"),sQuery(id+"F22.wireOp",EDGE,"E68"),sQuery(id+"F22.wireOp",EDGE,"E69"),sQuery(id+"F22.wireOp",EDGE,"E70"),sQuery(id+"F22.wireOp",EDGE,"E71"),sQuery(id+"F22.wireOp",EDGE,"E72"),sQuery(id+"F22.wireOp",EDGE,"E73"),sQuery(id+"F22.wireOp",EDGE,"E74"),sQuery(id+"F22.wireOp",EDGE,"E75"),sQuery(id+"F22.wireOp",EDGE,"E76")])]});
            hole(context, id + "F27", {"style" : HoleStyle.SIMPLE, "endStyle" : HoleEndStyle.BLIND, "standardTappedOrClearance" : lookupTablePath({ "standard" : "ISO", "fit" : "Normal", "size" : "M6", "type" : "Clearance" }), "standardBlindInLast" : lookupTablePath({ "fit" : "Standard", "standard" : "ISO", "size" : "M6", "type" : "Clearance" }), "holeDiameter" : 6.6 * mm, "holeDepth" : 12 * mm, "tappedDepth" : 12 * mm, "tapClearance" : 3, "locations" : qUnion([Q0, Q1]), "scope" : qUnion([Q2])});
        }
        {
            var Q0;
            Q0=makeQuery(id+"F21.opExtrude","CAP_FACE",FACE,{"disambiguationData":[OSD([sQuery(id+"F20.wireOp",EDGE,"E64.0"),sQuery(id+"F20.wireOp",EDGE,"E64.1"),sQuery(id+"F20.wireOp",EDGE,"E64.2"),sQuery(id+"F20.wireOp",EDGE,"E64.3"),sQuery(id+"F20.wireOp",EDGE,"E64.4"),sQuery(id+"F20.wireOp",EDGE,"E64.5")])],"isStart":true});
            var sketch = newSketch(context, id + "F28", { "sketchPlane" : qUnion([Q0])});
            skLineSegment(sketch, "E80.0.0", {"start": v(-29.23, 50.63) * mm, "end": v(-30.96, 47.63) * mm, "construction": true});
            skLineSegment(sketch, "E80.0.1", {"start": v(-30.96, 47.63) * mm, "end": v(-29.23, 44.63) * mm, "construction": true});
            skLineSegment(sketch, "E80.0.2", {"start": v(-29.23, 44.63) * mm, "end": v(-25.77, 44.63) * mm, "construction": true});
            skLineSegment(sketch, "E80.0.3", {"start": v(-25.77, 44.63) * mm, "end": v(-24.04, 47.63) * mm, "construction": true});
            skLineSegment(sketch, "E80.0.4", {"start": v(-24.04, 47.63) * mm, "end": v(-25.77, 50.63) * mm, "construction": true});
            skLineSegment(sketch, "E80.0.5", {"start": v(-25.77, 50.63) * mm, "end": v(-29.23, 50.63) * mm, "construction": true});
            skPoint(sketch, "E81", {"position": v(-27.5, 47.63) * mm});
            skPoint(sketch, "E81.positionSnap0", {"position": v(-27.5, 50.63) * mm});
            skSolve(sketch);
        }
        {
            var Q0;
            Q0=sQuery(id+"F28.wireOp",VERTEX,"E81");
            var Q1;
            Q1=makeQuery(id+"F21.opExtrude","SWEPT_BODY",BODY,{"disambiguationData":[OSD([sQuery(id+"F20.wireOp",EDGE,"E64.0"),sQuery(id+"F20.wireOp",EDGE,"E64.1"),sQuery(id+"F20.wireOp",EDGE,"E64.2"),sQuery(id+"F20.wireOp",EDGE,"E64.3"),sQuery(id+"F20.wireOp",EDGE,"E64.4"),sQuery(id+"F20.wireOp",EDGE,"E64.5")])]});
            hole(context, id + "F29", {"style" : HoleStyle.SIMPLE, "endStyle" : HoleEndStyle.BLIND, "standardTappedOrClearance" : lookupTablePath({ "standard" : "ISO", "engagement" : "75%", "pitch" : "0.5 mm", "size" : "M3", "type" : "Tapped" }), "standardBlindInLast" : lookupTablePath({ "standard" : "ISO", "engagement" : "75%", "pitch" : "0.5 mm", "size" : "M3", "type" : "Tapped" }), "holeDiameter" : 2.5 * mm, "showTappedDepth" : true, "holeDepth" : 13.5 * mm, "tappedDepth" : 12 * mm, "tapClearance" : 3, "locations" : qUnion([Q0]), "scope" : qUnion([Q1]), "majorDiameter" : 3 * mm});
        }
        {
            var Q0;
            Q0=makeQuery(id+"F21.opExtrude","CAP_FACE",FACE,{"disambiguationData":[OSD([sQuery(id+"F20.wireOp",EDGE,"E64.0"),sQuery(id+"F20.wireOp",EDGE,"E64.1"),sQuery(id+"F20.wireOp",EDGE,"E64.2"),sQuery(id+"F20.wireOp",EDGE,"E64.3"),sQuery(id+"F20.wireOp",EDGE,"E64.4"),sQuery(id+"F20.wireOp",EDGE,"E64.5")])],"isStart":true});
            var sketch = newSketch(context, id + "F30", { "sketchPlane" : qUnion([Q0])});
            skCircle(sketch, "E82", {"center": v(-27.5, 47.63) * mm, "radius": 3 * mm});
            skSolve(sketch);
        }
        {
            var Q0;
            Q0=makeQuery(id+"F30.imprint","IMPRINT",FACE,{"disambiguationData":[TD([[makeQuery(id+"F30.imprint","IMPRINT",EDGE,{"derivedFrom":sQuery(id+"F30.wireOp",EDGE,"E82")}),-1.0]])]});
            extrude(context, id + "F31", {"entities" : qUnion([Q0]), "operationType" : NewBodyOperationType.REMOVE, "oppositeDirection" : true, "depth" : 10 * mm});
        }
        {
            var Q0;
            Q0=qCreatedBy(makeId("Front.planeOp"),FACE);
            var sketch = newSketch(context, id + "F32", { "sketchPlane" : qUnion([Q0])});
            skLineSegment(sketch, "E83", {"start": v(-168.07, 63) * mm, "end": v(-149.57, 63) * mm, "construction": true});
            skLineSegment(sketch, "E84", {"start": v(0, 0) * mm, "end": v(-238.96, 0) * mm, "construction": true});
            skLineSegment(sketch, "E85", {"start": v(-158.82, 63) * mm, "end": v(-158.82, 0) * mm, "construction": true});
            skLineSegment(sketch, "E86", {"start": v(-158.82, 63) * mm, "end": v(-157.82, 63) * mm});
            skLineSegment(sketch, "E87", {"start": v(-157.82, 63) * mm, "end": v(-157.82, 60.83) * mm});
            skLineSegment(sketch, "E88", {"start": v(-157.82, 60.83) * mm, "end": v(-152.28, 60.83) * mm});
            skLineSegment(sketch, "E89", {"start": v(-152.28, 60.83) * mm, "end": v(-152.28, 63) * mm});
            skLineSegment(sketch, "E90", {"start": v(-152.28, 63) * mm, "end": v(-149.57, 63) * mm});
            skLineSegment(sketch, "E91.MirrorCS", {"start": v(-159.82, 63) * mm, "end": v(-159.82, 60.83) * mm});
            skLineSegment(sketch, "E92.MirrorCS", {"start": v(-159.82, 60.83) * mm, "end": v(-165.36, 60.83) * mm});
            skLineSegment(sketch, "E93.MirrorCS", {"start": v(-165.36, 60.83) * mm, "end": v(-165.36, 63) * mm});
            skLineSegment(sketch, "E94", {"start": v(-159.82, 63) * mm, "end": v(-158.82, 63) * mm});
            skLineSegment(sketch, "E95", {"start": v(-165.36, 63) * mm, "end": v(-168.07, 63) * mm});
            skLineSegment(sketch, "E96", {"start": v(-158.82, 0) * mm, "end": v(-157.32, 0) * mm});
            skLineSegment(sketch, "E97", {"start": v(-157.32, 0) * mm, "end": v(-157.32, 48) * mm});
            skLineSegment(sketch, "E98", {"start": v(-157.32, 48) * mm, "end": v(-149.57, 48) * mm});
            skLineSegment(sketch, "E99", {"start": v(-149.57, 48) * mm, "end": v(-149.57, 63) * mm});
            skLineSegment(sketch, "E100.MirrorCS", {"start": v(-160.32, 48) * mm, "end": v(-168.07, 48) * mm});
            skLineSegment(sketch, "E101.MirrorCS", {"start": v(-160.32, 0) * mm, "end": v(-160.32, 48) * mm});
            skLineSegment(sketch, "E102.MirrorCS", {"start": v(-168.07, 48) * mm, "end": v(-168.07, 63) * mm});
            skLineSegment(sketch, "E103", {"start": v(-160.32, 0) * mm, "end": v(-158.82, 0) * mm});
            skSolve(sketch);
        }
        {
            var Q0;
            Q0=makeQuery(id+"F32.imprint","IMPRINT",FACE,{"disambiguationData":[TD([[makeQuery(id+"F32.imprint","IMPRINT",EDGE,{"derivedFrom":sQuery(id+"F32.wireOp",EDGE,"E87")}),-1.0]])]});
            var Q1;
            Q1=sQuery(id+"F32.wireOp",EDGE,"E84");
            revolve(context, id + "F33", {"entities" : qUnion([Q0]), "axis" : qUnion([Q1]), "revolveType" : RevolveType.FULL});
        }
        {
            var Q0;
            Q0=makeQuery(id+"F33.opRevolve","SWEPT_EDGE",EDGE,{"disambiguationData":[OSD([sQuery(id+"F32.wireOp",EDGE,"E100.MirrorCS"),sQuery(id+"F32.wireOp",EDGE,"E102.MirrorCS")])]});
            var Q1;
            Q1=makeQuery(id+"F33.opRevolve","SWEPT_EDGE",EDGE,{"disambiguationData":[OSD([sQuery(id+"F32.wireOp",EDGE,"E98"),sQuery(id+"F32.wireOp",EDGE,"E99")])]});
            chamfer(context, id + "F34", {"entities" : qUnion([Q0, Q1]), "width" : 1 * mm, "tangentPropagation" : true});
        }
        {
            var Q0;
            Q0=makeQuery(id+"F33.opRevolve","SWEPT_EDGE",EDGE,{"disambiguationData":[OSD([sQuery(id+"F32.wireOp",EDGE,"E89"),sQuery(id+"F32.wireOp",EDGE,"E90")])]});
            var Q1;
            Q1=makeQuery(id+"F33.opRevolve","SWEPT_EDGE",EDGE,{"disambiguationData":[OSD([sQuery(id+"F32.wireOp",EDGE,"E87"),sQuery(id+"F32.wireOp",EDGE,"E86")])]});
            var Q2;
            Q2=makeQuery(id+"F33.opRevolve","SWEPT_EDGE",EDGE,{"disambiguationData":[OSD([sQuery(id+"F32.wireOp",EDGE,"E91.MirrorCS"),sQuery(id+"F32.wireOp",EDGE,"E94")])]});
            var Q3;
            Q3=makeQuery(id+"F33.opRevolve","SWEPT_EDGE",EDGE,{"disambiguationData":[OSD([sQuery(id+"F32.wireOp",EDGE,"E93.MirrorCS"),sQuery(id+"F32.wireOp",EDGE,"E95")])]});
            chamfer(context, id + "F35", {"entities" : qUnion([Q0, Q1, Q2, Q3]), "width" : .25 * mm, "tangentPropagation" : true});
        }
        {
            var Q0;
            Q0=makeQuery(id+"F33.opRevolve","SWEPT_FACE",FACE,{"disambiguationData":[OSD([sQuery(id+"F32.wireOp",EDGE,"E88")])]});
            var Q1;
            Q1=makeQuery(id+"F33.opRevolve","SWEPT_FACE",FACE,{"disambiguationData":[OSD([sQuery(id+"F32.wireOp",EDGE,"E92.MirrorCS")])]});
            fillet(context, id + "F36", {"entities" : qUnion([Q0, Q1]), "radius" : .2 * mm, "tangentPropagation" : true, "allowEdgeOverflow" : false});
        }
        {
            var Q0;
            Q0=makeQuery(id+"F33.opRevolve","SWEPT_EDGE",EDGE,{"disambiguationData":[OSD([sQuery(id+"F32.wireOp",EDGE,"E95"),sQuery(id+"F32.wireOp",EDGE,"E102.MirrorCS")])]});
            chamfer(context, id + "F37", {"entities" : qUnion([Q0]), "chamferType" : ChamferType.OFFSET_ANGLE, "width" : 2 * mm, "oppositeDirection" : false, "angle" : 10 * degree, "tangentPropagation" : true});
        }
        {
            var Q0;
            Q0=makeQuery(id+"F33.opRevolve","SWEPT_EDGE",EDGE,{"disambiguationData":[OSD([sQuery(id+"F32.wireOp",EDGE,"E90"),sQuery(id+"F32.wireOp",EDGE,"E99")])]});
            chamfer(context, id + "F38", {"entities" : qUnion([Q0]), "chamferType" : ChamferType.OFFSET_ANGLE, "width" : 2 * mm, "oppositeDirection" : true, "angle" : 10 * degree, "tangentPropagation" : true});
        }
        {
            var Q0;
            Q0=makeQuery(id+"F33.opRevolve","SWEPT_EDGE",EDGE,{"disambiguationData":[OSD([sQuery(id+"F32.wireOp",EDGE,"E100.MirrorCS"),sQuery(id+"F32.wireOp",EDGE,"E101.MirrorCS")])]});
            var Q1;
            Q1=makeQuery(id+"F33.opRevolve","SWEPT_EDGE",EDGE,{"disambiguationData":[OSD([sQuery(id+"F32.wireOp",EDGE,"E97"),sQuery(id+"F32.wireOp",EDGE,"E98")])]});
            chamfer(context, id + "F39", {"entities" : qUnion([Q0, Q1]), "width" : 1 * mm, "tangentPropagation" : true});
        }
        {
            var Q0;
            Q0=makeQuery(id+"F33.opRevolve","SWEPT_FACE",FACE,{"disambiguationData":[OSD([sQuery(id+"F32.wireOp",EDGE,"E102.MirrorCS")])]});
            var sketch = newSketch(context, id + "F40", { "sketchPlane" : qUnion([Q0])});
            skCircle(sketch, "E104.cCircle", {"center": v(0, 0) * mm, "radius": 51.5 * mm, "construction": true});
            skLineSegment(sketch, "E104.0", {"start": v(51.5, 0) * mm, "end": v(25.75, -44.6) * mm, "construction": true});
            skLineSegment(sketch, "E104.1", {"start": v(25.75, -44.6) * mm, "end": v(-25.75, -44.6) * mm, "construction": true});
            skLineSegment(sketch, "E104.2", {"start": v(-25.75, -44.6) * mm, "end": v(-51.5, 0) * mm, "construction": true});
            skLineSegment(sketch, "E104.3", {"start": v(-51.5, 0) * mm, "end": v(-25.75, 44.6) * mm, "construction": true});
            skLineSegment(sketch, "E104.4", {"start": v(-25.75, 44.6) * mm, "end": v(25.75, 44.6) * mm, "construction": true});
            skLineSegment(sketch, "E104.5", {"start": v(25.75, 44.6) * mm, "end": v(51.5, 0) * mm, "construction": true});
            skSolve(sketch);
        }
        {
            var Q0;
            Q0=makeQuery(id+"F33.opRevolve","SWEPT_FACE",FACE,{"disambiguationData":[OSD([sQuery(id+"F32.wireOp",EDGE,"E99")])]});
            var sketch = newSketch(context, id + "F41", { "sketchPlane" : qUnion([Q0])});
            skPoint(sketch, "E105.0", {"position": v(-25.75, 44.6) * mm});
            skPoint(sketch, "E105.1", {"position": v(-51.5, 0) * mm});
            skPoint(sketch, "E105.2", {"position": v(-25.75, -44.6) * mm});
            skPoint(sketch, "E105.3", {"position": v(25.75, -44.6) * mm});
            skPoint(sketch, "E105.4", {"position": v(51.5, 0) * mm});
            skPoint(sketch, "E105.5", {"position": v(25.75, 44.6) * mm});
            skSolve(sketch);
        }
        {
            var Q0;
            Q0=sQuery(id+"F40.wireOp",VERTEX,"E104.2.end");
            var Q1;
            Q1=sQuery(id+"F40.wireOp",VERTEX,"E104.4.start");
            var Q2;
            Q2=sQuery(id+"F40.wireOp",VERTEX,"E104.5.start");
            var Q3;
            Q3=sQuery(id+"F40.wireOp",VERTEX,"E104.0.start");
            var Q4;
            Q4=sQuery(id+"F40.wireOp",VERTEX,"E104.0.end");
            var Q5;
            Q5=sQuery(id+"F40.wireOp",VERTEX,"E104.1.end");
            var Q6;
            Q6=sQuery(id+"F41.wireOp",VERTEX,"E105.0");
            var Q7;
            Q7=sQuery(id+"F41.wireOp",VERTEX,"E105.1");
            var Q8;
            Q8=sQuery(id+"F41.wireOp",VERTEX,"E105.2");
            var Q9;
            Q9=sQuery(id+"F41.wireOp",VERTEX,"E105.3");
            var Q10;
            Q10=sQuery(id+"F41.wireOp",VERTEX,"E105.4");
            var Q11;
            Q11=sQuery(id+"F41.wireOp",VERTEX,"E105.5");
            var Q12;
            Q12=makeQuery(id+"F33.opRevolve","SWEPT_BODY",BODY,{"disambiguationData":[OSD([sQuery(id+"F32.wireOp",EDGE,"E87"),sQuery(id+"F32.wireOp",EDGE,"E88"),sQuery(id+"F32.wireOp",EDGE,"E89"),sQuery(id+"F32.wireOp",EDGE,"E86"),sQuery(id+"F32.wireOp",EDGE,"E90"),sQuery(id+"F32.wireOp",EDGE,"E91.MirrorCS"),sQuery(id+"F32.wireOp",EDGE,"E92.MirrorCS"),sQuery(id+"F32.wireOp",EDGE,"E93.MirrorCS"),sQuery(id+"F32.wireOp",EDGE,"E94"),sQuery(id+"F32.wireOp",EDGE,"E95"),sQuery(id+"F32.wireOp",EDGE,"E96"),sQuery(id+"F32.wireOp",EDGE,"E97"),sQuery(id+"F32.wireOp",EDGE,"E98"),sQuery(id+"F32.wireOp",EDGE,"E99"),sQuery(id+"F32.wireOp",EDGE,"E100.MirrorCS"),sQuery(id+"F32.wireOp",EDGE,"E101.MirrorCS"),sQuery(id+"F32.wireOp",EDGE,"E102.MirrorCS"),sQuery(id+"F32.wireOp",EDGE,"E103")])]});
            hole(context, id + "F42", {"style" : HoleStyle.SIMPLE, "endStyle" : HoleEndStyle.BLIND, "standardTappedOrClearance" : lookupTablePath({ "standard" : "ISO", "engagement" : "75%", "pitch" : "0.5 mm", "size" : "M3", "type" : "Tapped" }), "standardBlindInLast" : lookupTablePath({ "standard" : "ISO", "engagement" : "75%", "pitch" : "0.5 mm", "size" : "M3", "type" : "Tapped" }), "holeDiameter" : 2.5 * mm, "showTappedDepth" : true, "holeDepth" : 6 * mm, "tappedDepth" : 5 * mm, "tapClearance" : 2, "locations" : qUnion([Q0, Q1, Q2, Q3, Q4, Q5, Q6, Q7, Q8, Q9, Q10, Q11]), "scope" : qUnion([Q12]), "majorDiameter" : 3 * mm});
        }
        {
            var Q0;
            Q0=makeQuery(id+"F21.opExtrude","CAP_FACE",FACE,{"disambiguationData":[OSD([sQuery(id+"F20.wireOp",EDGE,"E64.0"),sQuery(id+"F20.wireOp",EDGE,"E64.1"),sQuery(id+"F20.wireOp",EDGE,"E64.2"),sQuery(id+"F20.wireOp",EDGE,"E64.3"),sQuery(id+"F20.wireOp",EDGE,"E64.4"),sQuery(id+"F20.wireOp",EDGE,"E64.5")])],"isStart":false});
            var sketch = newSketch(context, id + "F43", { "sketchPlane" : qUnion([Q0])});
            skPoint(sketch, "E106", {"position": v(27.5, 47.63) * mm});
            skPoint(sketch, "E106.positionSnap0", {"position": v(27.5, 50.63) * mm});
            skSolve(sketch);
        }
        {
            var Q0;
            Q0=sQuery(id+"F43.wireOp",VERTEX,"E106");
            var Q1;
            Q1=makeQuery(id+"F21.opExtrude","SWEPT_BODY",BODY,{"disambiguationData":[OSD([sQuery(id+"F20.wireOp",EDGE,"E64.0"),sQuery(id+"F20.wireOp",EDGE,"E64.1"),sQuery(id+"F20.wireOp",EDGE,"E64.2"),sQuery(id+"F20.wireOp",EDGE,"E64.3"),sQuery(id+"F20.wireOp",EDGE,"E64.4"),sQuery(id+"F20.wireOp",EDGE,"E64.5")])]});
            hole(context, id + "F44", {"style" : HoleStyle.SIMPLE, "endStyle" : HoleEndStyle.BLIND, "standardTappedOrClearance" : lookupTablePath({ "standard" : "ISO", "engagement" : "75%", "pitch" : "0.5 mm", "size" : "M3", "type" : "Tapped" }), "standardBlindInLast" : lookupTablePath({ "standard" : "ISO", "engagement" : "75%", "pitch" : "0.5 mm", "size" : "M3", "type" : "Tapped" }), "holeDiameter" : 2.5 * mm, "showTappedDepth" : true, "holeDepth" : 12 * mm, "tappedDepth" : 11 * mm, "tapClearance" : 2, "locations" : qUnion([Q0]), "scope" : qUnion([Q1]), "majorDiameter" : 3 * mm});
        }
        {
            var Q0;
            Q0=makeQuery(id+"F18.opExtrude","CAP_FACE",FACE,{"disambiguationData":[OSD([sQuery(id+"F17.wireOp",EDGE,"E61"),sQuery(id+"F17.wireOp",EDGE,"E62")])],"isStart":true});
            cPlane(context, id + "F45", {"entities" : qUnion([Q0]), "cplaneType" : CPlaneType.OFFSET, "offset" : 9 * mm, "oppositeDirection" : true, "width" : 150 * mm, "height" : 150 * mm});
        }
        {
            var Q0;
            Q0=makeQuery(id+"F18.opExtrude","CAP_FACE",FACE,{"disambiguationData":[OSD([sQuery(id+"F17.wireOp",EDGE,"E61"),sQuery(id+"F17.wireOp",EDGE,"E62")])],"isStart":false});
            cPlane(context, id + "F46", {"entities" : qUnion([Q0]), "cplaneType" : CPlaneType.OFFSET, "offset" : 9 * mm, "oppositeDirection" : true, "width" : 150 * mm, "height" : 150 * mm});
        }
        {
            var Q0;
            Q0=qCreatedBy(id+"F45.planeOp",FACE);
            var sketch = newSketch(context, id + "F47", { "sketchPlane" : qUnion([Q0])});
            skCircle(sketch, "E107.0", {"center": v(0, 0) * mm, "radius": 69.85 * mm, "construction": true});
            skLineSegment(sketch, "E108", {"start": v(0, 0) * mm, "end": v(26.73, 64.53) * mm, "construction": true});
            skLineSegment(sketch, "E109", {"start": v(0, 0) * mm, "end": v(0, 69.85) * mm});
            skLineSegment(sketch, "E110.1.0", {"start": v(0, 0) * mm, "end": v(-26.73, 64.53) * mm, "construction": true});
            skLineSegment(sketch, "E110.2.0", {"start": v(0, 0) * mm, "end": v(-64.53, 26.73) * mm, "construction": true});
            skLineSegment(sketch, "E110.3.0", {"start": v(0, 0) * mm, "end": v(-64.53, -26.73) * mm, "construction": true});
            skLineSegment(sketch, "E110.4.0", {"start": v(0, 0) * mm, "end": v(-26.73, -64.53) * mm, "construction": true});
            skLineSegment(sketch, "E110.5.0", {"start": v(0, 0) * mm, "end": v(26.73, -64.53) * mm, "construction": true});
            skLineSegment(sketch, "E110.6.0", {"start": v(0, 0) * mm, "end": v(64.53, -26.73) * mm, "construction": true});
            skLineSegment(sketch, "E110.7.0", {"start": v(0, 0) * mm, "end": v(64.53, 26.73) * mm, "construction": true});
            skSolve(sketch);
        }
        {
            var Q0;
            Q0=qCreatedBy(id+"F46.planeOp",FACE);
            var sketch = newSketch(context, id + "F48", { "sketchPlane" : qUnion([Q0])});
            skPoint(sketch, "E111.0", {"position": v(0, 0) * mm});
            skSolve(sketch);
        }
        {
            var Q0;
            Q0=sQuery(id+"F47.wireOp",EDGE,"E108");
            var Q1;
            Q1=sQuery(id+"F47.wireOp",VERTEX,"E108.end");
            cPlane(context, id + "F49", {"entities" : qUnion([Q0, Q1]), "cplaneType" : CPlaneType.LINE_POINT, "offset" : 25 * mm, "width" : 150 * mm, "height" : 150 * mm});
        }
        {
            var Q0;
            Q0=sQuery(id+"F47.wireOp",EDGE,"E110.7.0");
            var Q1;
            Q1=sQuery(id+"F47.wireOp",VERTEX,"E110.7.0.end");
            cPlane(context, id + "F50", {"entities" : qUnion([Q0, Q1]), "cplaneType" : CPlaneType.LINE_POINT, "offset" : 25 * mm, "width" : 150 * mm, "height" : 150 * mm});
        }
        {
            var Q0;
            Q0=sQuery(id+"F47.wireOp",EDGE,"E110.6.0");
            var Q1;
            Q1=sQuery(id+"F47.wireOp",VERTEX,"E110.6.0.end");
            cPlane(context, id + "F51", {"entities" : qUnion([Q0, Q1]), "cplaneType" : CPlaneType.LINE_POINT, "offset" : 25 * mm, "width" : 150 * mm, "height" : 150 * mm});
        }
        {
            var Q0;
            Q0=sQuery(id+"F47.wireOp",EDGE,"E110.5.0");
            var Q1;
            Q1=sQuery(id+"F47.wireOp",VERTEX,"E110.5.0.end");
            cPlane(context, id + "F52", {"entities" : qUnion([Q0, Q1]), "cplaneType" : CPlaneType.LINE_POINT, "offset" : 25 * mm, "width" : 150 * mm, "height" : 150 * mm});
        }
        {
            var Q0;
            Q0=sQuery(id+"F47.wireOp",EDGE,"E110.4.0");
            var Q1;
            Q1=sQuery(id+"F47.wireOp",VERTEX,"E110.4.0.end");
            cPlane(context, id + "F53", {"entities" : qUnion([Q0, Q1]), "cplaneType" : CPlaneType.LINE_POINT, "offset" : 25 * mm, "width" : 150 * mm, "height" : 150 * mm});
        }
        {
            var Q0;
            Q0=sQuery(id+"F47.wireOp",EDGE,"E110.3.0");
            var Q1;
            Q1=sQuery(id+"F47.wireOp",VERTEX,"E110.3.0.end");
            cPlane(context, id + "F54", {"entities" : qUnion([Q0, Q1]), "cplaneType" : CPlaneType.LINE_POINT, "offset" : 25 * mm, "width" : 150 * mm, "height" : 150 * mm});
        }
        {
            var Q0;
            Q0=sQuery(id+"F47.wireOp",EDGE,"E110.2.0");
            var Q1;
            Q1=sQuery(id+"F47.wireOp",VERTEX,"E110.2.0.end");
            cPlane(context, id + "F55", {"entities" : qUnion([Q0, Q1]), "cplaneType" : CPlaneType.LINE_POINT, "offset" : 25 * mm, "width" : 150 * mm, "height" : 150 * mm});
        }
        {
            var Q0;
            Q0=sQuery(id+"F47.wireOp",EDGE,"E110.1.0");
            var Q1;
            Q1=sQuery(id+"F47.wireOp",VERTEX,"E110.1.0.end");
            cPlane(context, id + "F56", {"entities" : qUnion([Q0, Q1]), "cplaneType" : CPlaneType.LINE_POINT, "offset" : 25 * mm, "width" : 150 * mm, "height" : 150 * mm});
        }
        {
            var Q0;
            Q0=qCreatedBy(id+"F50.planeOp",FACE);
            var sketch = newSketch(context, id + "F57", { "sketchPlane" : qUnion([Q0])});
            skPoint(sketch, "E112.0", {"position": v(-266, 0) * mm});
            skPoint(sketch, "E113.0", {"position": v(116, 0) * mm});
            skSolve(sketch);
        }
        {
            var Q0;
            Q0=qCreatedBy(id+"F49.planeOp",FACE);
            var sketch = newSketch(context, id + "F58", { "sketchPlane" : qUnion([Q0])});
            skPoint(sketch, "E114.0", {"position": v(-266, 0) * mm});
            skPoint(sketch, "E114.1", {"position": v(116, 0) * mm});
            skSolve(sketch);
        }
        {
            var Q0;
            Q0=qCreatedBy(id+"F51.planeOp",FACE);
            var sketch = newSketch(context, id + "F59", { "sketchPlane" : qUnion([Q0])});
            skPoint(sketch, "E115.0", {"position": v(-266, 0) * mm});
            skPoint(sketch, "E115.1", {"position": v(116, 0) * mm});
            skSolve(sketch);
        }
        {
            var Q0;
            Q0=qCreatedBy(id+"F52.planeOp",FACE);
            var sketch = newSketch(context, id + "F60", { "sketchPlane" : qUnion([Q0])});
            skPoint(sketch, "E116.0", {"position": v(-266, 0) * mm});
            skPoint(sketch, "E116.1", {"position": v(116, 0) * mm});
            skSolve(sketch);
        }
        {
            var Q0;
            Q0=qCreatedBy(id+"F53.planeOp",FACE);
            var sketch = newSketch(context, id + "F61", { "sketchPlane" : qUnion([Q0])});
            skPoint(sketch, "E117.0", {"position": v(-266, 0) * mm});
            skPoint(sketch, "E117.1", {"position": v(116, 0) * mm});
            skSolve(sketch);
        }
        {
            var Q0;
            Q0=qCreatedBy(id+"F54.planeOp",FACE);
            var sketch = newSketch(context, id + "F62", { "sketchPlane" : qUnion([Q0])});
            skPoint(sketch, "E118.0", {"position": v(266, 0) * mm});
            skPoint(sketch, "E118.1", {"position": v(-116, 0) * mm});
            skSolve(sketch);
        }
        {
            var Q0;
            Q0=qCreatedBy(id+"F55.planeOp",FACE);
            var sketch = newSketch(context, id + "F63", { "sketchPlane" : qUnion([Q0])});
            skPoint(sketch, "E119.0", {"position": v(266, 0) * mm});
            skPoint(sketch, "E119.1", {"position": v(-116, 0) * mm});
            skSolve(sketch);
        }
        {
            var Q0;
            Q0=qCreatedBy(id+"F56.planeOp",FACE);
            var sketch = newSketch(context, id + "F64", { "sketchPlane" : qUnion([Q0])});
            skPoint(sketch, "E120.0", {"position": v(-266, 0) * mm});
            skPoint(sketch, "E120.1", {"position": v(116, 0) * mm});
            skSolve(sketch);
        }
        {
            var Q0;
            Q0=sQuery(id+"F58.wireOp",VERTEX,"E114.0");
            var Q1;
            Q1=sQuery(id+"F64.wireOp",VERTEX,"E120.0");
            var Q2;
            Q2=sQuery(id+"F63.wireOp",VERTEX,"E119.0");
            var Q3;
            Q3=sQuery(id+"F62.wireOp",VERTEX,"E118.0");
            var Q4;
            Q4=sQuery(id+"F61.wireOp",VERTEX,"E117.0");
            var Q5;
            Q5=sQuery(id+"F60.wireOp",VERTEX,"E116.0");
            var Q6;
            Q6=sQuery(id+"F59.wireOp",VERTEX,"E115.0");
            var Q7;
            Q7=sQuery(id+"F57.wireOp",VERTEX,"E112.0");
            var Q8;
            Q8=sQuery(id+"F61.wireOp",VERTEX,"E117.1");
            var Q9;
            Q9=sQuery(id+"F60.wireOp",VERTEX,"E116.1");
            var Q10;
            Q10=sQuery(id+"F59.wireOp",VERTEX,"E115.1");
            var Q11;
            Q11=sQuery(id+"F57.wireOp",VERTEX,"E113.0");
            var Q12;
            Q12=sQuery(id+"F58.wireOp",VERTEX,"E114.1");
            var Q13;
            Q13=sQuery(id+"F64.wireOp",VERTEX,"E120.1");
            var Q14;
            Q14=sQuery(id+"F63.wireOp",VERTEX,"E119.1");
            var Q15;
            Q15=sQuery(id+"F62.wireOp",VERTEX,"E118.1");
            var Q16;
            Q16=makeQuery(id+"F18.opExtrude","SWEPT_BODY",BODY,{"disambiguationData":[OSD([sQuery(id+"F17.wireOp",EDGE,"E61"),sQuery(id+"F17.wireOp",EDGE,"E62")])]});
            hole(context, id + "F65", {"style" : HoleStyle.SIMPLE, "endStyle" : HoleEndStyle.BLIND, "holeDiameter" : 6 * mm, "holeDepth" : 12 * mm, "tappedDepth" : 12 * mm, "tapClearance" : 3, "locations" : qUnion([Q0, Q1, Q2, Q3, Q4, Q5, Q6, Q7, Q8, Q9, Q10, Q11, Q12, Q13, Q14, Q15]), "scope" : qUnion([Q16])});
        }
    });
